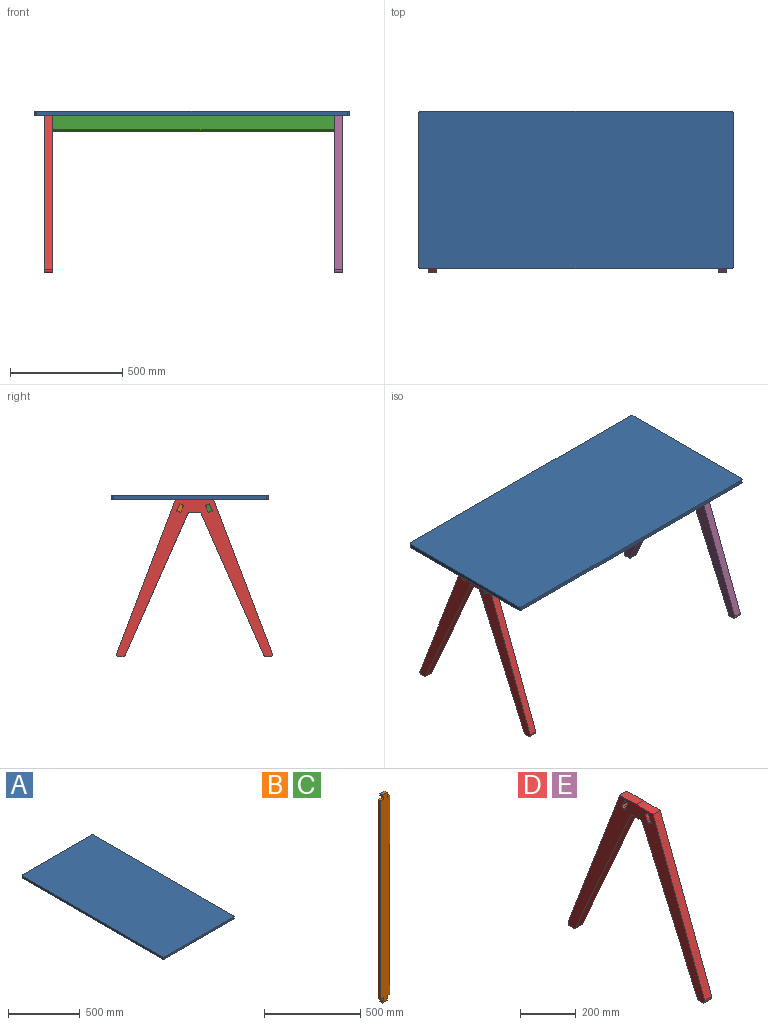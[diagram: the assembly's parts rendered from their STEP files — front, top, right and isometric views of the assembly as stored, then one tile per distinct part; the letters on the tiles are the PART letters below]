
ASSEMBLY  parts=5 mates=3
PART A: 10 faces, bbox 700x1400x18 mm
  f0: plane 1382.5x18mm, normal (1,0,0), area 24885mm2, adj f1,f7,f8,f9
  f1: cylinder r=8.75mm len=18mm, axis (0,0,-1), area 247.4mm2, adj f0,f2,f8,f9
  f2: plane 682.5x18mm, normal (0,1,0), area 12285mm2, adj f1,f3,f8,f9
  f3: cylinder r=8.75mm len=18mm, axis (0,0,-1), area 247.4mm2, adj f2,f4,f8,f9
  f4: plane 1382.5x18mm, normal (-1,0,0), area 24885mm2, adj f3,f5,f8,f9
  f5: cylinder r=8.75mm len=18mm, axis (0,0,-1), area 247.4mm2, adj f4,f6,f8,f9
  f6: plane 682.5x18mm, normal (0,-1,0), area 12285mm2, adj f5,f7,f8,f9
  f7: cylinder r=8.75mm len=18mm, axis (0,0,-1), area 247.4mm2, adj f0,f6,f8,f9
  f8: plane 1400x700mm, normal (0,0,1), area 979934.4mm2, adj f0,f1,f2,f3,f4,f5,f6,f7
  f9: plane 1400x700mm, normal (0,0,-1), area 979934.4mm2, adj f0,f1,f2,f3,f4,f5,f6,f7
PART B: 34 faces, bbox 70x18x1324.8 mm
  f0: plane 1263.03x18mm, normal (-1,0,0), area 22734.6mm2, adj f1,f31,f32,f33
  f1: cylinder r=1mm len=18mm, axis (0,1,0), area 28.3mm2, adj f0,f2,f32,f33
  f2: plane 18x17.34mm, normal (0,0,-1), area 312.2mm2, adj f1,f3,f32,f33
  f3: cylinder r=4mm len=18mm, axis (0,1,0), area 226.2mm2, adj f2,f4,f32,f33
  f4: plane 18x5.69mm, normal (-1,0,0), area 102.4mm2, adj f3,f5,f32,f33
  f5: cylinder r=4mm len=18mm, axis (0,1,0), area 226.2mm2, adj f4,f6,f32,f33
  f6: plane 18x2.34mm, normal (0,0,1), area 42.2mm2, adj f5,f7,f32,f33
  f7: cylinder r=2mm len=18mm, axis (0,1,0), area 56.5mm2, adj f6,f8,f32,f33
  f8: plane 18x8.88mm, normal (-1,0,0), area 159.9mm2, adj f7,f9,f32,f33
  f9: cylinder r=2mm len=18mm, axis (0,1,0), area 56.5mm2, adj f8,f10,f32,f33
  f10: plane 31.24x18mm, normal (0,0,-1), area 562.3mm2, adj f9,f11,f32,f33
  f11: cylinder r=2mm len=18mm, axis (0,1,0), area 56.5mm2, adj f10,f12,f32,f33
  f12: plane 23.24x18mm, normal (1,0,0), area 418.4mm2, adj f11,f13,f32,f33
  f13: cylinder r=4mm len=18mm, axis (0,1,0), area 226.2mm2, adj f12,f14,f32,f33
  f14: plane 18x13.09mm, normal (0,0,-1), area 235.7mm2, adj f13,f15,f32,f33
  f15: cylinder r=2mm len=18mm, axis (0,1,0), area 56.5mm2, adj f14,f16,f32,f33
  f16: plane 1259.03x18mm, normal (1,0,0), area 22662.6mm2, adj f15,f17,f32,f33
  f17: cylinder r=2mm len=18mm, axis (0,1,0), area 56.5mm2, adj f16,f18,f32,f33
  f18: plane 18x13.09mm, normal (0,0,1), area 235.7mm2, adj f17,f19,f32,f33
  f19: cylinder r=4mm len=18mm, axis (0,1,0), area 223.8mm2, adj f18,f20,f32,f33
  f20: plane 23.34x18mm, normal (1,0,0), area 420.1mm2, adj f19,f21,f32,f33
  f21: cylinder r=2mm len=18mm, axis (0,1,0), area 56.5mm2, adj f20,f22,f32,f33
  f22: plane 31.15x18mm, normal (0,0,1), area 560.7mm2, adj f21,f23,f32,f33
  f23: cylinder r=2mm len=18mm, axis (0,1,0), area 56.5mm2, adj f22,f24,f32,f33
  f24: plane 18x8.9mm, normal (-1,0,0), area 160.2mm2, adj f23,f25,f32,f33
  f25: cylinder r=2mm len=18mm, axis (0,1,0), area 56.5mm2, adj f24,f26,f32,f33
  f26: plane 18x2.34mm, normal (0,0,-1), area 42.2mm2, adj f25,f27,f32,f33
  f27: cylinder r=4mm len=18mm, axis (0,1,0), area 226.2mm2, adj f26,f28,f32,f33
  f28: plane 18x6.69mm, normal (-1,0,0), area 120.4mm2, adj f27,f29,f32,f33
  f29: cylinder r=4mm len=18mm, axis (0,1,0), area 248.6mm2, adj f28,f30,f32,f33
  f30: plane 18x16.61mm, normal (0,0,1), area 299.1mm2, adj f29,f31,f32,f33
  f31: cylinder r=1mm len=18mm, axis (0,1,0), area 28.3mm2, adj f0,f30,f32,f33
  f32: plane 1324.83x70mm, normal (0,-1,0), area 90207.7mm2, adj f0,f1,f2,f3,f4,f5,f6,f7
  f33: plane 1324.83x70mm, normal (0,1,0), area 90207.7mm2, adj f0,f1,f2,f3,f4,f5,f6,f7
PART C: same geometry as B
PART D: 38 faces, bbox 36x694.1x702 mm
  f0: plane 702.04x694.13mm, normal (-1,0,0), area 86384.5mm2, adj f1,f2,f3,f4,f5,f6,f7,f8
  f1: plane 36x27mm, normal (0,0,-1), area 971.9mm2, adj f0,f2,f18,f19
  f2: plane 36x0mm, normal (0,-0.85,0.53), area 0.2mm2, adj f0,f1,f3,f19
  f3: plane 638.9x282.02mm, normal (0,-0.91,-0.4), area 25141.4mm2, adj f0,f2,f4,f19
  f4: cylinder r=10mm len=36mm, axis (-1,0,0), area 415.8mm2, adj f0,f3,f5,f19
  f5: plane 36x18.89mm, normal (0,0,-1), area 680.2mm2, adj f0,f4,f6,f19
  f6: cylinder r=10mm len=36mm, axis (-1,0,0), area 696.3mm2, adj f0,f5,f7,f19
  f7: plane 688.47x261.77mm, normal (0,0.93,0.36), area 26516.1mm2, adj f0,f6,f8,f19
  f8: plane 82.88x36mm, normal (0,0,1), area 2983.7mm2, adj f0,f7,f9,f19
  f9: plane 36x0mm, normal (0,0.6,-0.8), area 0mm2, adj f0,f8,f10,f19
  f10: plane 36x1.76mm, normal (0,0,1), area 63.3mm2, adj f0,f9,f11,f19
  f11: plane 84.64x36mm, normal (0,0,1), area 3046.9mm2, adj f0,f10,f12,f19
  f12: plane 688.47x261.78mm, normal (0,-0.93,0.36), area 26516.1mm2, adj f0,f11,f13,f19
  f13: cylinder r=10mm len=36mm, axis (-1,0,0), area 696.3mm2, adj f0,f12,f14,f19
  f14: plane 36x18.89mm, normal (0,0,-1), area 680.2mm2, adj f0,f13,f15,f19
  f15: cylinder r=10mm len=36mm, axis (-1,0,0), area 415.8mm2, adj f0,f14,f16,f19
  f16: plane 636.51x280.97mm, normal (0,0.91,-0.4), area 25047.5mm2, adj f0,f15,f17,f19
  f17: cylinder r=4mm len=36mm, axis (-1,0,0), area 166.3mm2, adj f0,f16,f18,f19
  f18: plane 36x24.39mm, normal (0,0,-1), area 878mm2, adj f0,f1,f17,f19
  f19: plane 702.04x694.13mm, normal (1,0,0), area 87734.9mm2, adj f1,f2,f3,f4,f5,f6,f7,f8
  f20: cylinder r=4mm len=30mm, axis (-1,0,0), area 378.8mm2, adj f0,f21,f27,f28
  f21: plane 30x6.16mm, normal (0,0.39,-0.92), area 200.5mm2, adj f0,f20,f22,f28
  f22: cylinder r=4mm len=30mm, axis (-1,0,0), area 378.6mm2, adj f0,f21,f23,f28
  f23: plane 30x22.61mm, normal (0,0.92,0.39), area 738.2mm2, adj f0,f22,f24,f28
  f24: cylinder r=4mm len=30mm, axis (-1,0,0), area 378.6mm2, adj f0,f23,f25,f28
  f25: plane 30x5.8mm, normal (0,-0.39,0.92), area 188.5mm2, adj f0,f24,f26,f28
  f26: cylinder r=4mm len=30mm, axis (-1,0,0), area 378.8mm2, adj f0,f25,f27,f28
  f27: plane 30x22.77mm, normal (0,-0.93,-0.38), area 738.1mm2, adj f0,f20,f26,f28
  f28: plane 40.67x30.93mm, normal (-1,0,0), area 675.2mm2, adj f20,f21,f22,f23,f24,f25,f26,f27
  f29: plane 30x6.16mm, normal (0,-0.39,-0.92), area 200.5mm2, adj f0,f30,f36,f37
  f30: cylinder r=4mm len=30mm, axis (-1,0,0), area 378.8mm2, adj f0,f29,f31,f37
  f31: plane 30x22.77mm, normal (0,0.93,-0.38), area 738.1mm2, adj f0,f30,f32,f37
  f32: cylinder r=4mm len=30mm, axis (-1,0,0), area 378.8mm2, adj f0,f31,f33,f37
  f33: plane 30x5.8mm, normal (0,0.39,0.92), area 188.5mm2, adj f0,f32,f34,f37
  f34: cylinder r=4mm len=30mm, axis (-1,0,0), area 378.6mm2, adj f0,f33,f35,f37
  f35: plane 30x22.61mm, normal (0,-0.92,0.39), area 738.2mm2, adj f0,f34,f36,f37
  f36: cylinder r=4mm len=30mm, axis (-1,0,0), area 378.6mm2, adj f0,f29,f35,f37
  f37: plane 40.67x30.93mm, normal (-1,0,0), area 675.2mm2, adj f29,f30,f31,f32,f33,f34,f35,f36
PART E: same geometry as D
PLACE A rot(axis=(0,0,-1),90deg) t=(234.97,665.88,554.26)mm
PLACE B rot(axis=(0.19,-0.96,-0.19),92.2deg) t=(241.56,716.63,520.32)mm fixed
PLACE C rot(axis=(-0.19,-0.96,0.19),92.2deg) t=(241.56,592.68,513.37)mm fixed
PLACE D rot(axis=(0,0,1),180deg) t=(-383.95,646.36,202.59)mm
PLACE E t=(867.58,646.35,202.59)mm fixed
MATE planar C.f28 <-> D.f25  axis (0,-0.39,-0.92) through (-398.95,580.13,506.7)mm
MATE planar C.f4 <-> E.f33  axis (0,-0.39,-0.92) through (882.58,580.13,506.7)mm
MATE planar B.f4 <-> E.f25  axis (0,0.39,-0.92) through (882.58,712.58,506.7)mm
